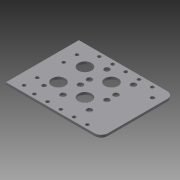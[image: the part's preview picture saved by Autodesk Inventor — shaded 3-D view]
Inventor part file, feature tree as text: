
AUTODESK INVENTOR PART (.ipt)
format: ipt  version: 2015 (Build 190159000, 159)  size: 161,792 bytes
history: native  units: in
note: dims shown in document units (in); Inventor stores cm internally (conversion verified against a paired STEP export)
features: extrude x5, sketch x4, pattern_linear x2, plane x1, hole x1, fillet x1, projected_geometry x1
ambient origin geometry x8: Origin, YZ Plane, XZ Plane, XY Plane, X Axis, Y Axis, Z Axis, Center Point
bodies: Solid1 (feature_tree)
feature tree (15):
  plane  "Work Plane1"
  extrude  "Extrusion1"  Depth=2.75in
  extrude  "Extrusion2"  Depth=0.09in TaperAngle=0.0deg
  hole  "Hole1"  [1 undecoded]
  pattern_linear  "Rectangular Pattern1"  Count1=5 Spacing1=0.5in
  sketch  "Sketch6"  dims[d7=0.15in d8=0.15in]
  extrude  "Extrusion4"  Depth=0.09in TaperAngle=0.0deg
  fillet  "Fillet2"  Radius=0.25in
  extrude  "Extrusion5"  Depth=0.09in TaperAngle=0.0deg
  extrude  "Extrusion6"  Depth=0.09in
  pattern_linear  "Rectangular Pattern2"  Spacing1=0.5in  [1 undecoded]
  sketch  "Sketch1"  dims[d0=2.75in d1=3.5in]
  projected_geometry  "Projected Loop1"
  sketch  "Sketch3"  dims[d2=0.09in d3=0.0in d5=0.09in d6=0.0in]
  sketch  "Sketch8"  dims[d9=0.129in d10=0.75in d11=0.375in d12=0.25in d13=0.5635in d14=0.09in d15=0.8108in d16=1.9685in d18=0.5in d22=0.09in d23=0.0in d24=0.25in d25=0.09in d26=0.0in d27=0.5in d33=0.5in d34=0.33in d35=0.33in d36=1.0in d37=0.0in d38=0.7874in d40=1.0in d41=0.7874in d43=1.0in]
note: 2 required parameter values undecoded (feature->parameter linkage not recoverable at this tier; creation-order binding heuristic only, values carry confidence <= 0.55)
